# Revit family: NLRS_33_GM_FB_TC_STORAX_vloerluik_BV-GDZ_BCB
name_source: partatom
category: Generic Models
revit_build: Autodesk Revit 2014 (Build: 20130308_1515(x64)
units: mm (PartAtom-declared; Revit-internal decimal feet)

## types (5) — shared parameters
Default Elevation = 1219 mm
Manufacturer = Storax
Model = BV
URL = http://www.storax.nl
belasting = 125 kN
binnenluik = tbv betonvulling
brandwerend 90 min = nee
gasdrukveer = ja
geïsoleerd = nee
materiaal = bcb_staal
productgroep = Vloerluiken
rubberen_afdichting = enkel
scharnierend = ja
sluiting = 1
vergrendeling = nee
vullen_met_beton = ja

## per-type parameters (varying)
| type | binnenmaat_breedte | binnenmaat_lengte | gasveer 2 | gewicht | uitwendige_breedte | uitwendige_lengte |
| BV-GDZ 66 | 600 mm | 600 mm | No | 30 | 735 mm | 752 mm  [stored 2.46719 ft] |
| BV-GDZ 86 | 800 mm  [stored 2.62467 ft] | 600 mm | Yes | 38 | 935 mm | 752 mm  [stored 2.46719 ft] |
| BV-GDZ 88 | 800 mm  [stored 2.62467 ft] | 800 mm  [stored 2.62467 ft] | Yes | 44 | 935 mm | 952 mm  [stored 3.12336 ft] |
| BV-GDZ 110 | 1000 mm  [stored 3.28084 ft] | 1000 mm  [stored 3.28084 ft] | Yes | 58 | 1135 mm  [stored 3.72375 ft] | 1152 mm  [stored 3.77953 ft] |
| maatwerk | 1000 mm  [stored 3.28084 ft] | 1000 mm  [stored 3.28084 ft] | Yes | 0 | 1135 mm  [stored 3.72375 ft] | 1152 mm  [stored 3.77953 ft] |

note: [stored X ft] marks values corroborated as IEEE doubles in the binary element streams (Revit-internal decimal feet)

## geometry (parser evidence)
native form markers: Blend x781, Sweep x11
no freeform markers — native parametric forms only
